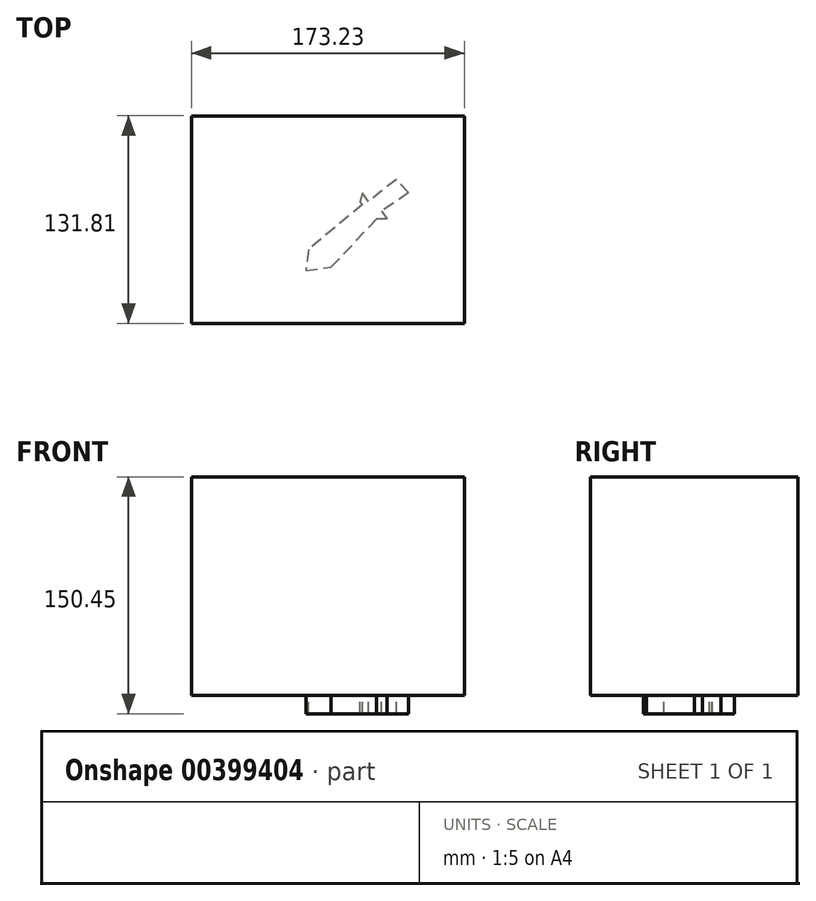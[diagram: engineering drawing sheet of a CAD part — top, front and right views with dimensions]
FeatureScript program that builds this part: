
annotation { "Feature Type Name" : "Feature", "Feature Type Description" : "" }
export const myFeature = defineFeature(function(context is Context, id is Id, definition is map)
    precondition{}
    {
        {
            var Q0;
            Q0=qCreatedBy(makeId("Right.planeOp"),FACE);
            var sketch = newSketch(context, id + "F0", { "sketchPlane" : qUnion([Q0])});
            skLineSegment(sketch, "E0.bottom", {"start": v(108.47, 63.07) * mm, "end": v(-23.34, 63.07) * mm});
            skLineSegment(sketch, "E0.top", {"start": v(108.47, -75.7) * mm, "end": v(-23.34, -75.7) * mm});
            skLineSegment(sketch, "E0.left", {"start": v(108.47, 63.07) * mm, "end": v(108.47, -75.7) * mm});
            skLineSegment(sketch, "E0.right", {"start": v(-23.34, 63.07) * mm, "end": v(-23.34, -75.7) * mm});
            skSolve(sketch);
        }
        {
            var Q0;
            Q0=makeQuery(id+"F0.imprint","IMPRINT",FACE,{"disambiguationData":[TD([[makeQuery(id+"F0.imprint","IMPRINT",EDGE,{"derivedFrom":sQuery(id+"F0.wireOp",EDGE,"E0.bottom")}),1.0]])]});
            extrude(context, id + "F1", {"entities" : qUnion([Q0]), "depth" : 173.23 * mm});
        }
        {
            var Q0;
            Q0=makeQuery(id+"F1.opExtrude","SWEPT_FACE",FACE,{"disambiguationData":[OSD([sQuery(id+"F0.wireOp",EDGE,"E0.top")])]});
            var sketch = newSketch(context, id + "F2", { "sketchPlane" : qUnion([Q0])});
            skLineSegment(sketch, "E1", {"start": v(137.9, -59.61) * mm, "end": v(130.03, -68.1) * mm});
            skLineSegment(sketch, "E2", {"start": v(130.03, -68.1) * mm, "end": v(112.23, -54.1) * mm});
            skLineSegment(sketch, "E3", {"start": v(137.9, -59.61) * mm, "end": v(120.64, -47.84) * mm});
            skLineSegment(sketch, "E4", {"start": v(112.23, -54.1) * mm, "end": v(108.58, -59.46) * mm});
            skLineSegment(sketch, "E5", {"start": v(120.64, -47.84) * mm, "end": v(124.04, -42.85) * mm});
            skLineSegment(sketch, "E6", {"start": v(108.58, -59.46) * mm, "end": v(106.96, -53.93) * mm});
            skLineSegment(sketch, "E7", {"start": v(124.04, -42.85) * mm, "end": v(117.5, -42.85) * mm});
            skLineSegment(sketch, "E8", {"start": v(117.5, -42.85) * mm, "end": v(106.96, -53.93) * mm});
            skLineSegment(sketch, "E9", {"start": v(108.58, -52.24) * mm, "end": v(74.17, -23.45) * mm});
            skLineSegment(sketch, "E10", {"start": v(74.17, -23.45) * mm, "end": v(72.53, -10.27) * mm});
            skLineSegment(sketch, "E11", {"start": v(72.53, -10.27) * mm, "end": v(88.67, -12.41) * mm});
            skLineSegment(sketch, "E12", {"start": v(88.67, -12.41) * mm, "end": v(117.5, -42.85) * mm});
            skSolve(sketch);
        }
        {
            var Q0;
            {var subQ0=sQuery(id+"F2.wireOp",EDGE,"E9");Q0=makeQuery(id+"F2.imprint","IMPRINT",FACE,{"disambiguationData":[TD([[makeQuery(id+"F2.imprint","IMPRINT",EDGE,{"derivedFrom":subQ0}),-1.0]])]});}
            var Q1;
            Q1=makeQuery(id+"F2.imprint","IMPRINT",FACE,{"disambiguationData":[TD([[makeQuery(id+"F2.imprint","IMPRINT",EDGE,{"derivedFrom":sQuery(id+"F2.wireOp",EDGE,"E1")}),-1.0]])]});
            extrude(context, id + "F3", {"entities" : qUnion([Q0, Q1]), "operationType" : NewBodyOperationType.ADD, "depth" : 11.68 * mm});
        }
    });
